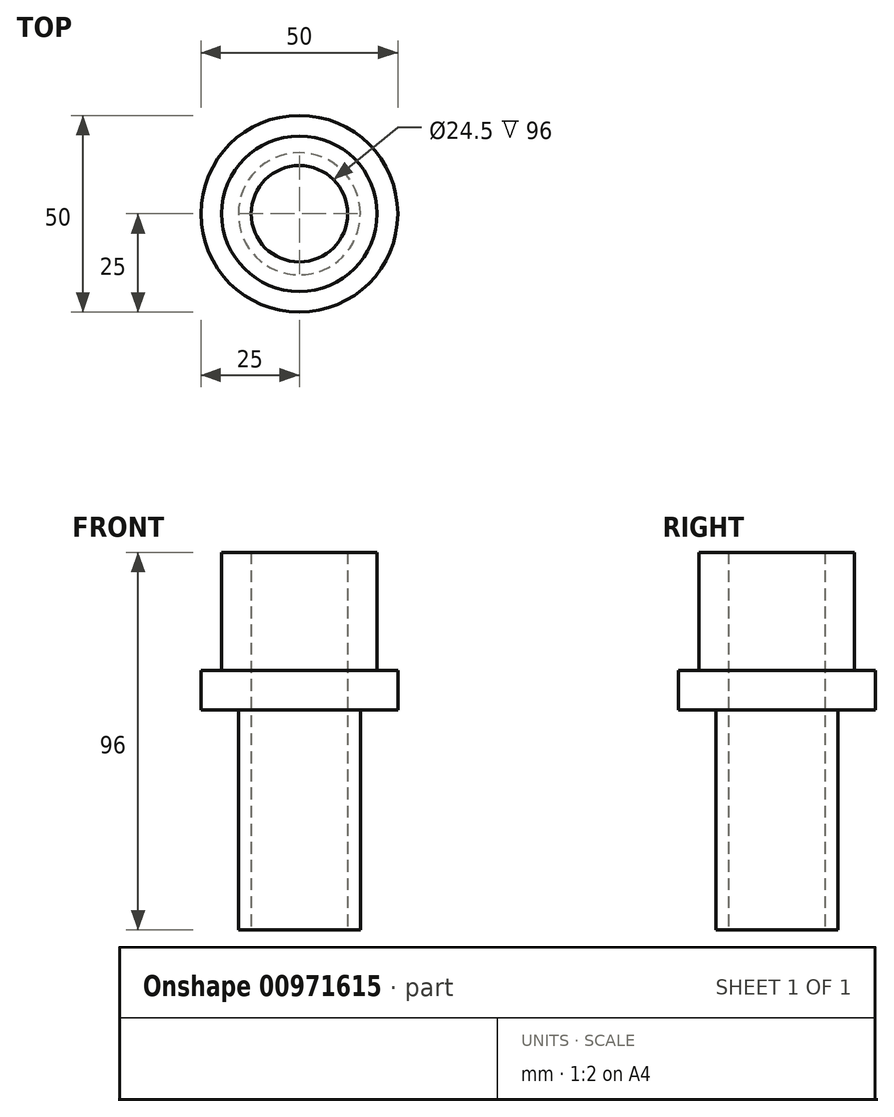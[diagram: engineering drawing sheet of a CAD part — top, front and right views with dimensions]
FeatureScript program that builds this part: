
annotation { "Feature Type Name" : "Feature", "Feature Type Description" : "" }
export const myFeature = defineFeature(function(context is Context, id is Id, definition is map)
    precondition{}
    {
        {
            var Q0;
            Q0=qCreatedBy(makeId("Top.planeOp"),FACE);
            var sketch = newSketch(context, id + "F0", { "sketchPlane" : qUnion([Q0])});
            skCircle(sketch, "E0", {"center": v(0, 0) * mm, "radius": 19.75 * mm});
            skLineSegment(sketch, "E1", {"start": v(0, 0) * mm, "end": v(-19.75, 0) * mm});
            skCircle(sketch, "E2", {"center": v(0, 0) * mm, "radius": 12.25 * mm});
            skSolve(sketch);
        }
        {
            var Q0;
            Q0=makeQuery(id+"F0.imprint","IMPRINT",FACE,{"disambiguationData":[TD([[makeQuery(id+"F0.imprint","IMPRINT",EDGE,{"derivedFrom":sQuery(id+"F0.wireOp",EDGE,"E0")}),1.0]])]});
            var Q1;
            Q1=sQuery(id+"F0.wireOp",EDGE,"E0");
            var Q2;
            Q2=sQuery(id+"F0.wireOp",EDGE,"E2");
            extrude(context, id + "F1", {"entities" : qUnion([Q0]), "surfaceEntities" : qUnion([Q1, Q2]), "depth" : 30 * mm, "offsetDistance" : 25 * mm});
        }
        {
            var Q0;
            Q0=qCreatedBy(makeId("Top.planeOp"),FACE);
            var sketch = newSketch(context, id + "F2", { "sketchPlane" : qUnion([Q0])});
            skCircle(sketch, "E3", {"center": v(0, 0) * mm, "radius": 15.5 * mm});
            skLineSegment(sketch, "E4", {"start": v(0, 0) * mm, "end": v(15.5, 0) * mm});
            skCircle(sketch, "E5", {"center": v(0, 0) * mm, "radius": 12.25 * mm});
            skSolve(sketch);
        }
        {
            var Q0;
            Q0 = qSketchRegion(id + "F2", true);
            var Q1;
            Q1 = qSketchRegion(id + "F4", true);
            extrude(context, id + "F3", {"entities" : qUnion([Q0, Q1]), "operationType" : NewBodyOperationType.ADD, "oppositeDirection" : true, "depth" : 66 * mm, "offsetDistance" : 25 * mm});
        }
        {
            var Q0;
            Q0=qCreatedBy(makeId("Top.planeOp"),FACE);
            var sketch = newSketch(context, id + "F4", { "sketchPlane" : qUnion([Q0])});
            skCircle(sketch, "E6", {"center": v(0, 0) * mm, "radius": 25 * mm});
            skLineSegment(sketch, "E7", {"start": v(0, 0) * mm, "end": v(0, -25) * mm});
            skCircle(sketch, "E8", {"center": v(0, 0) * mm, "radius": 12.25 * mm});
            skSolve(sketch);
        }
        {
            var Q0;
            Q0 = qSketchRegion(id + "F4", true);
            extrude(context, id + "F5", {"entities" : qUnion([Q0]), "operationType" : NewBodyOperationType.ADD, "oppositeDirection" : true, "depth" : 10 * mm, "offsetDistance" : 25 * mm});
        }
    });
